# Revit family: Infire_Inside C version 1
name_source: partatom
category: Zabudowa
revit_build: Autodesk Revit 2018 (Build: 20180329_1100(x64)
units: mm (PartAtom-declared; Revit-internal decimal feet)

## family parameters
Numer OmniClass = 23.40.20.34.14
Obiekt nadrzędny = Powierzchnia
Punkt obliczania pomieszczeń = Nie
Tnij formami wycięć po wczytaniu = Nie
Tytuł OmniClass = Fireplaces
Współdzielony = Nie

## types (3) — shared parameters
Domyślna rzędna = 1000 mm  [stored 3.28084 ft]
Grubość blachy = 2 mm  [stored 0.00656168 ft]
Gwarancja = 24 miesiące
Głębokość = 250 mm  [stored 0.82021 ft]
IfcExportAs = IfcSpaceHeaterType
Komentarze do typu = Biokominek
Materiał (obudowa) = INFIRE - czarny
Materiał (szkło) = INFIRE - szkło
Model = INSIDE C1000 version 1
Obraz typu = Infire_Inside C1000 v1.jpg
Producent = INFIRE Biokominki
Szkło = Szyba hartowana 4 mm, przyciemniana
URL = http://www.infire.pl
Wysokość = 450 mm  [stored 1.47638 ft]

## per-type parameters (varying)
| type | Grubość paleniska | Rozstaw mocowania | Szerokość | Szerokość paleniska | Szerokość szyby | Wysokość szyby |
| INSIDE C1000 version 1 | 165 mm | 730 mm | 1000 mm  [stored 3.28084 ft] | 790 mm | 800 mm  [stored 2.62467 ft] | 100 mm  [stored 0.328084 ft] |
| INSIDE C1200 version 1 | 203 mm | 940 mm | 1200 mm | 1000 mm  [stored 3.28084 ft] | 1100 mm | 120 mm  [stored 0.393701 ft] |
| INSIDE C800 version 1 | 155 mm  [stored 0.50853 ft] | 460 mm | 800 mm  [stored 2.62467 ft] | 520 mm  [stored 1.70604 ft] | 660 mm  [stored 2.16535 ft] | 100 mm  [stored 0.328084 ft] |

note: [stored X ft] marks values corroborated as IEEE doubles in the binary element streams (Revit-internal decimal feet)
